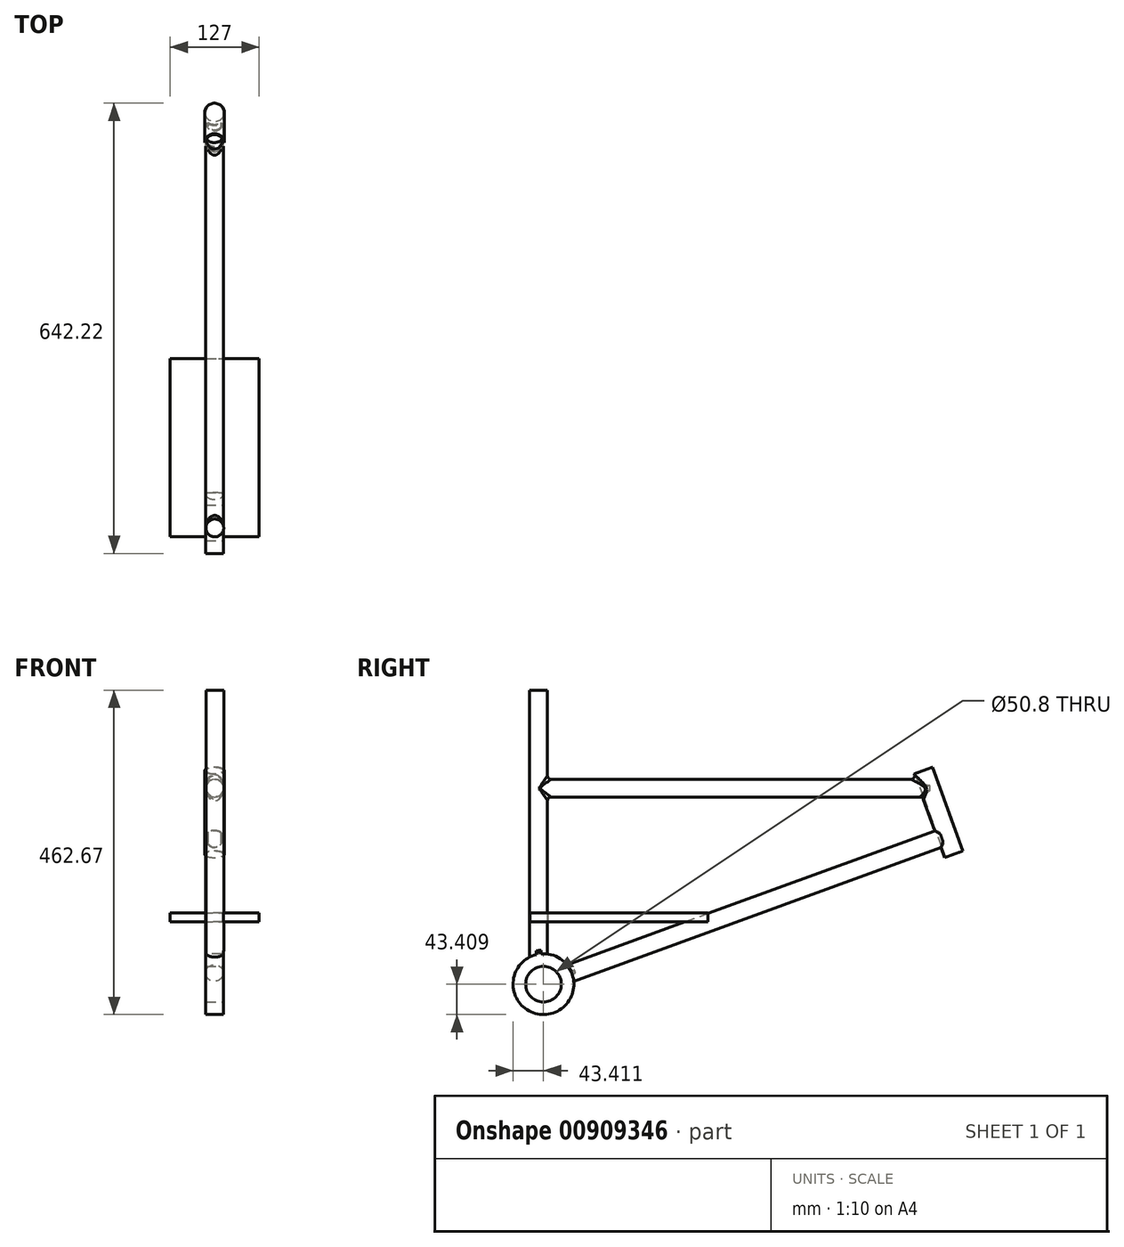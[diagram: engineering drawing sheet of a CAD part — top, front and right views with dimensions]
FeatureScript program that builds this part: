
annotation { "Feature Type Name" : "Feature", "Feature Type Description" : "" }
export const myFeature = defineFeature(function(context is Context, id is Id, definition is map)
    precondition{}
    {
        {
            var Q0;
            Q0=qCreatedBy(makeId("Top.planeOp"),FACE);
            var sketch = newSketch(context, id + "F0", { "sketchPlane" : qUnion([Q0])});
            skCircle(sketch, "E0", {"center": v(0, 71) * mm, "radius": 12.7 * mm});
            skCircle(sketch, "E1", {"center": v(0, 71) * mm, "radius": 13.97 * mm});
            skSolve(sketch);
        }
        {
            var Q0;
            Q0=makeQuery(id+"F0.imprint","IMPRINT",FACE,{"disambiguationData":[TD([[makeQuery(id+"F0.imprint","IMPRINT",EDGE,{"derivedFrom":sQuery(id+"F0.wireOp",EDGE,"E0")}),-1.0]])]});
            extrude(context, id + "F1", {"entities" : qUnion([Q0]), "depth" : 63.5 * mm, "offsetDistance" : 25 * mm, "hasSecondDirection" : true, "secondDirectionOppositeDirection" : true, "secondDirectionDepth" : 63.5 * mm});
        }
        {
            var Q0;
            Q0=qCreatedBy(makeId("Right.planeOp"),FACE);
            cPlane(context, id + "F2", {"entities" : qUnion([Q0]), "cplaneType" : CPlaneType.OFFSET, "offset" : 6.5 * mm, "width" : 150 * mm, "height" : 150 * mm});
        }
        {
            var Q0;
            Q0=qCreatedBy(makeId("Front.planeOp"),FACE);
            cPlane(context, id + "F3", {"entities" : qUnion([Q0]), "cplaneType" : CPlaneType.OFFSET, "offset" : 64.5 * mm, "oppositeDirection" : true, "width" : 150 * mm, "height" : 150 * mm});
        }
        {
            var Q0;
            Q0=qCreatedBy(id+"F3.planeOp",FACE);
            var sketch = newSketch(context, id + "F4", { "sketchPlane" : qUnion([Q0])});
            skLineSegment(sketch, "E2", {"start": v(0.63, 25.04) * mm, "end": v(0.63, -24.88) * mm});
            skLineSegment(sketch, "E3", {"start": v(0.63, -0.08) * mm, "end": v(-5.5, -0.08) * mm});
            skPoint(sketch, "E3.startSnap0", {"position": v(0.63, 0.08) * mm});
            skLineSegment(sketch, "E4", {"start": v(-5.5, -0.08) * mm, "end": v(7.89, -0.08) * mm});
            skSolve(sketch);
        }
        {
            var Q0;
            Q0=makeQuery(id+"F1.opExtrude","SWEPT_BODY",BODY,{"disambiguationData":[OSD([sQuery(id+"F0.wireOp",EDGE,"E0"),sQuery(id+"F0.wireOp",EDGE,"E1")])]});
            var Q1;
            Q1=sQuery(id+"F4.wireOp",EDGE,"E4");
            transform(context, id + "F5", {"entities" : qUnion([Q0]), "transformType" : TransformType.ROTATION, "transformAxis" : qUnion([Q1]), "angle" : 20 * degree, "makeCopy" : false});
        }
        {
            var Q0;
            Q0=qCreatedBy(makeId("Front.planeOp"),FACE);
            var sketch = newSketch(context, id + "F6", { "sketchPlane" : qUnion([Q0])});
            skCircle(sketch, "E5", {"center": v(0.3, 36.86) * mm, "radius": 12.7 * mm});
            skSolve(sketch);
        }
        {
            var Q0;
            Q0=makeQuery(id+"F6.imprint","IMPRINT",FACE,{"disambiguationData":[TD([[makeQuery(id+"F6.imprint","IMPRINT",EDGE,{"derivedFrom":sQuery(id+"F6.wireOp",EDGE,"E5")}),1.0]])]});
            extrude(context, id + "F7", {"entities" : qUnion([Q0]), "operationType" : NewBodyOperationType.ADD, "depth" : 500.38 * mm, "offsetDistance" : 25.4 * mm, "hasSecondDirection" : true, "secondDirectionOppositeDirection" : true, "secondDirectionDepth" : 58.42 * mm});
        }
        {
            var Q0;
            Q0=qCreatedBy(makeId("Top.planeOp"),FACE);
            var sketch = newSketch(context, id + "F8", { "sketchPlane" : qUnion([Q0])});
            skCircle(sketch, "E6", {"center": v(42.78, -48.43) * mm, "radius": 12.7 * mm});
            skSolve(sketch);
        }
        {
            var Q0;
            Q0=makeQuery(id+"F8.imprint","IMPRINT",FACE,{"disambiguationData":[TD([[makeQuery(id+"F8.imprint","IMPRINT",EDGE,{"derivedFrom":sQuery(id+"F8.wireOp",EDGE,"E6")}),1.0]])]});
            extrude(context, id + "F9", {"entities" : qUnion([Q0]), "depth" : 279.4 * mm, "offsetDistance" : 25.4 * mm, "hasSecondDirection" : true, "secondDirectionOppositeDirection" : true, "secondDirectionDepth" : 279.4 * mm});
        }
        {
            var Q0;
            Q0=makeQuery(id+"F9.opExtrude","SWEPT_BODY",BODY,{"disambiguationData":[OSD([sQuery(id+"F8.wireOp",EDGE,"E6")])]});
            var Q1;
            {var subQ0=sQuery(id+"F6.wireOp",EDGE,"E5");Q1=makeQuery(id+"F7.boolean.opBoolean","SPLIT",FACE,{"disambiguationData":[TD([makeQuery(id+"F1.opExtrude","SWEPT_FACE",FACE,{"disambiguationData":[OSD([sQuery(id+"F0.wireOp",EDGE,"E1")])]})])],"derivedFrom":makeQuery(id+"F7.opExtrude","SWEPT_FACE",FACE,{"disambiguationData":[OSD([subQ0])]})});}
            transform(context, id + "F10", {"entities" : qUnion([Q0]), "transformType" : TransformType.ROTATION, "transformAxis" : qUnion([Q1]), "angle" : 90 * degree, "makeCopy" : false});
        }
        {
            var Q0;
            Q0=makeQuery(id+"F9.opExtrude","SWEPT_BODY",BODY,{"disambiguationData":[OSD([sQuery(id+"F8.wireOp",EDGE,"E6")])]});
            var Q1;
            Q1=makeQuery(id+"F1.opExtrude","SWEPT_FACE",FACE,{"disambiguationData":[OSD([sQuery(id+"F0.wireOp",EDGE,"E1")])]});
            transform(context, id + "F11", {"entities" : qUnion([Q0]), "transformType" : TransformType.ROTATION, "transformAxis" : qUnion([Q1]), "angle" : 90 * degree, "makeCopy" : false});
        }
        {
            var Q0;
            Q0=makeQuery(id+"F9.opExtrude","SWEPT_BODY",BODY,{"disambiguationData":[OSD([sQuery(id+"F8.wireOp",EDGE,"E6")])]});
            transform(context, id + "F12", {"entities" : qUnion([Q0]), "transformType" : TransformType.TRANSLATION_3D, "dx" : 114.3 * mm, "dy" : -287.02 * mm, "dz" : -177.8 * mm, "makeCopy" : false});
        }
        {
            var Q0;
            Q0=makeQuery(id+"F9.opExtrude","CAP_FACE",FACE,{"disambiguationData":[OSD([sQuery(id+"F8.wireOp",EDGE,"E6")])],"isStart":true});
            extrude(context, id + "F13", {"entities" : qUnion([Q0]), "operationType" : NewBodyOperationType.ADD, "depth" : 6.35 * mm, "offsetDistance" : 25.4 * mm});
        }
        {
            var Q0;
            Q0=makeQuery(id+"F1.opExtrude","CAP_FACE",FACE,{"disambiguationData":[OSD([sQuery(id+"F0.wireOp",EDGE,"E0"),sQuery(id+"F0.wireOp",EDGE,"E1")])],"isStart":false});
            cPlane(context, id + "F14", {"entities" : qUnion([Q0]), "cplaneType" : CPlaneType.OFFSET, "offset" : 0 * mm, "width" : 152.4 * mm, "height" : 152.4 * mm});
        }
        {
            var Q0;
            Q0=qCreatedBy(id+"F14.planeOp",FACE);
            var sketch = newSketch(context, id + "F15", { "sketchPlane" : qUnion([Q0])});
            skCircle(sketch, "E7", {"center": v(0, 67.14) * mm, "radius": 12.57 * mm});
            skSolve(sketch);
        }
        {
            var Q0;
            Q0=makeQuery(id+"F15.imprint","IMPRINT",FACE,{"disambiguationData":[TD([[makeQuery(id+"F15.imprint","IMPRINT",EDGE,{"derivedFrom":sQuery(id+"F15.wireOp",EDGE,"E7")}),1.0]])]});
            extrude(context, id + "F16", {"entities" : qUnion([Q0]), "operationType" : NewBodyOperationType.REMOVE, "endBound" : BoundingType.THROUGH_ALL, "oppositeDirection" : true, "depth" : 25.4 * mm, "offsetDistance" : 25.4 * mm});
        }
        {
            var Q0;
            Q0=qCreatedBy(makeId("Top.planeOp"),FACE);
            cPlane(context, id + "F17", {"entities" : qUnion([Q0]), "cplaneType" : CPlaneType.OFFSET, "offset" : 49.53 * mm, "width" : 152.4 * mm, "height" : 152.4 * mm});
        }
        {
            var Q0;
            Q0=qCreatedBy(id+"F17.planeOp",FACE);
            var sketch = newSketch(context, id + "F18", { "sketchPlane" : qUnion([Q0])});
            skCircle(sketch, "E8", {"center": v(0.48, -500.33) * mm, "radius": 12.7 * mm});
            skSolve(sketch);
        }
        {
            var Q0;
            Q0=makeQuery(id+"F18.imprint","IMPRINT",FACE,{"disambiguationData":[TD([[makeQuery(id+"F18.imprint","IMPRINT",EDGE,{"derivedFrom":sQuery(id+"F18.wireOp",EDGE,"E8")}),1.0]])]});
            extrude(context, id + "F19", {"entities" : qUnion([Q0]), "operationType" : NewBodyOperationType.ADD, "depth" : 127 * mm, "offsetDistance" : 25.4 * mm, "hasSecondDirection" : true, "secondDirectionOppositeDirection" : true, "secondDirectionDepth" : 330.2 * mm});
        }
        {
            var Q0;
            Q0=qCreatedBy(makeId("Right.planeOp"),FACE);
            cPlane(context, id + "F20", {"entities" : qUnion([Q0]), "cplaneType" : CPlaneType.OFFSET, "offset" : 12.7 * mm, "width" : 152.4 * mm, "height" : 152.4 * mm});
        }
        {
            var Q0;
            Q0=qCreatedBy(id+"F20.planeOp",FACE);
            var sketch = newSketch(context, id + "F21", { "sketchPlane" : qUnion([Q0])});
            skCircle(sketch, "E9", {"center": v(-493.38, -242.73) * mm, "radius": 43.4 * mm});
            skCircle(sketch, "E10", {"center": v(-493.38, -242.73) * mm, "radius": 25.4 * mm});
            skSolve(sketch);
        }
        {
            var Q0;
            Q0=makeQuery(id+"F21.imprint","IMPRINT",FACE,{"disambiguationData":[TD([[makeQuery(id+"F21.imprint","IMPRINT",EDGE,{"derivedFrom":sQuery(id+"F21.wireOp",EDGE,"E9")}),1.0]])]});
            var Q1;
            Q1=makeQuery(id+"F21.imprint","IMPRINT",FACE,{"disambiguationData":[TD([[makeQuery(id+"F21.imprint","IMPRINT",EDGE,{"derivedFrom":sQuery(id+"F21.wireOp",EDGE,"E10")}),1.0]])]});
            extrude(context, id + "F22", {"entities" : qUnion([Q0, Q1]), "operationType" : NewBodyOperationType.REMOVE, "oppositeDirection" : true, "depth" : 27.94 * mm, "offsetDistance" : 25.4 * mm, "hasSecondDirection" : true, "secondDirectionOppositeDirection" : false, "secondDirectionDepth" : 27.94 * mm});
        }
        {
            var Q0;
            Q0=makeQuery(id+"F21.imprint","IMPRINT",FACE,{"disambiguationData":[TD([[makeQuery(id+"F21.imprint","IMPRINT",EDGE,{"derivedFrom":sQuery(id+"F21.wireOp",EDGE,"E9")}),1.0]])]});
            extrude(context, id + "F23", {"entities" : qUnion([Q0]), "operationType" : NewBodyOperationType.ADD, "oppositeDirection" : true, "depth" : 25.4 * mm, "offsetDistance" : 25.4 * mm});
        }
        {
            var Q0;
            {var subQ0=sQuery(id+"F6.wireOp",EDGE,"E5");Q0=makeQuery(id+"F19.boolean.opBoolean","INTERSECT",EDGE,{"derivedFrom":[makeQuery(id+"F7.boolean.opBoolean","SPLIT",FACE,{"disambiguationData":[TD([makeQuery(id+"F1.opExtrude","SWEPT_FACE",FACE,{"disambiguationData":[OSD([sQuery(id+"F0.wireOp",EDGE,"E1")])]})])],"derivedFrom":makeQuery(id+"F7.opExtrude","SWEPT_FACE",FACE,{"disambiguationData":[OSD([subQ0])]})}),makeQuery(id+"F19.opExtrude","SWEPT_FACE",FACE,{"disambiguationData":[OSD([sQuery(id+"F18.wireOp",EDGE,"E8")])]})]});}
            var Q1;
            {var subQ0=makeQuery(id+"F19.opExtrude","SWEPT_FACE",FACE,{"disambiguationData":[OSD([sQuery(id+"F18.wireOp",EDGE,"E8")])]});var subQ1=sQuery(id+"F21.wireOp",EDGE,"E9");Q1=makeQuery(id+"F23.boolean.opBoolean","SPLIT",EDGE,{"disambiguationData":[topologyDisambiguationEdgeConnected([makeQuery(id+"F23.opExtrude","SWEPT_FACE",FACE,{"disambiguationData":[OSD([subQ1])]})])],"derivedFrom":makeQuery(id+"F22.boolean.opBoolean","INTERSECT",EDGE,{"derivedFrom":[subQ0,makeQuery(id+"F22.opExtrude","SWEPT_FACE",FACE,{"disambiguationData":[OSD([subQ1])]})]})});}
            var Q2;
            {var subQ0=sQuery(id+"F8.wireOp",EDGE,"E6");var subQ1=makeQuery(id+"F9.opExtrude","SWEPT_FACE",FACE,{"disambiguationData":[OSD([subQ0])]});var subQ2=makeQuery(id+"F13.opExtrude","SWEPT_FACE",FACE,{"disambiguationData":[OSD([subQ0])]});var subQ3=sQuery(id+"F21.wireOp",EDGE,"E9");Q2=makeQuery(id+"F23.boolean.opBoolean","SPLIT",EDGE,{"disambiguationData":[topologyDisambiguationEdgeConnected([makeQuery(id+"F23.opExtrude","SWEPT_FACE",FACE,{"disambiguationData":[OSD([subQ3])]})])],"derivedFrom":makeQuery(id+"F22.boolean.opBoolean","INTERSECT",EDGE,{"derivedFrom":[makeQuery(id+"F13.boolean.opBoolean","MERGE",FACE,{"disambiguationData":[OD(0.0)],"derivedFrom":[subQ1,subQ2]}),makeQuery(id+"F22.opExtrude","SWEPT_FACE",FACE,{"disambiguationData":[OSD([subQ3])]})]})});}
            var Q3;
            Q3=makeQuery(id+"F7.boolean.opBoolean","INTERSECT",EDGE,{"derivedFrom":[makeQuery(id+"F1.opExtrude","SWEPT_FACE",FACE,{"disambiguationData":[OSD([sQuery(id+"F0.wireOp",EDGE,"E1")])]}),makeQuery(id+"F7.opExtrude","SWEPT_FACE",FACE,{"disambiguationData":[OSD([sQuery(id+"F6.wireOp",EDGE,"E5")])]})]});
            fillet(context, id + "F24", {"entities" : qUnion([Q0, Q1, Q2, Q3]), "radius" : 5.08 * mm, "tangentPropagation" : true, "allowEdgeOverflow" : false});
        }
        {
            var Q0;
            Q0=qCreatedBy(makeId("Top.planeOp"),FACE);
            var sketch = newSketch(context, id + "F25", { "sketchPlane" : qUnion([Q0])});
            skLineSegment(sketch, "E11.bottom", {"start": v(19.58, -45.32) * mm, "end": v(146.58, -45.32) * mm});
            skLineSegment(sketch, "E11.top", {"start": v(19.58, -299.32) * mm, "end": v(146.58, -299.32) * mm});
            skLineSegment(sketch, "E11.left", {"start": v(19.58, -45.32) * mm, "end": v(19.58, -299.32) * mm});
            skLineSegment(sketch, "E11.right", {"start": v(146.58, -45.32) * mm, "end": v(146.58, -299.32) * mm});
            skLineSegment(sketch, "E12", {"start": v(83.08, -299.32) * mm, "end": v(83.08, -286.62) * mm});
            skCircle(sketch, "E13", {"center": v(83.08, -286.62) * mm, "radius": 12.7 * mm});
            skLineSegment(sketch, "E14", {"start": v(95.78, -286.62) * mm, "end": v(95.78, -299.32) * mm});
            skLineSegment(sketch, "E15", {"start": v(70.38, -286.62) * mm, "end": v(70.38, -299.32) * mm});
            skSolve(sketch);
        }
        {
            var Q0;
            Q0=makeQuery(id+"F25.imprint","IMPRINT",FACE,{"disambiguationData":[TD([[makeQuery(id+"F25.imprint","IMPRINT",EDGE,{"derivedFrom":sQuery(id+"F25.wireOp",EDGE,"E11.bottom")}),-1.0]])]});
            extrude(context, id + "F26", {"entities" : qUnion([Q0]), "depth" : 12.7 * mm, "offsetDistance" : 25.4 * mm});
        }
        {
            var Q0;
            Q0=makeQuery(id+"F26.opExtrude","SWEPT_BODY",BODY,{"disambiguationData":[OSD([sQuery(id+"F25.wireOp",EDGE,"E11.bottom"),sQuery(id+"F25.wireOp",EDGE,"E11.top"),sQuery(id+"F25.wireOp",EDGE,"E11.left"),sQuery(id+"F25.wireOp",EDGE,"E11.right")])]});
            transform(context, id + "F27", {"entities" : qUnion([Q0]), "transformType" : TransformType.TRANSLATION_3D, "dx" : -82.8 * mm, "dy" : -213.36 * mm, "dz" : -153.92 * mm, "makeCopy" : false});
        }
    });
